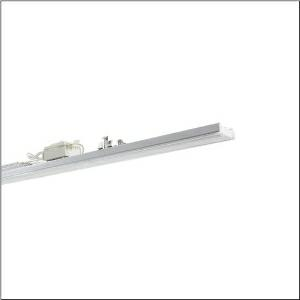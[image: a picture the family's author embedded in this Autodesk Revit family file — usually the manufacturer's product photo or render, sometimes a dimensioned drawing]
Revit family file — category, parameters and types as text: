
# Revit family: licross_r__21_recessed_ho_52te11mn4fxs_d685
name_source: partatom
category: Lighting Fixtures
units: mm (PartAtom-declared; Revit-internal decimal feet)

## family parameters
Cut with Voids When Loaded = No
Host = Face
Light Source = No
Part Type = Normal
Room Calculation Point = No
Round Connector Dimension = Use Diameter
Shared = No

## types (1)
- --- (1 x LED, 15070 lm, 83.1 W, 4000K)
    Apparent Load = 83 VA
    CIE Flux Codes = 87 95 99 100 100
    Color Rendering = 80
    Color Temperature = 4000K
    Default Elevation = 1800 mm
    Description = Licross® 21 Recessed HO, luminaire insert, of sheet steel, galvanised, coil coated, white, length: 1.500mm, width: 66mm, height: 67mm, LED rated luminous flux: 15.060lm, light colour: 840, control gear: ON/OFF Multilumen, with plug, 3-pole, with phase selection, mains connection: 220..240V, AC, 50/60Hz, rated input power: 83W, internal wiring halogen-free, primary light control with lens, of plastic, primary optical cover: cover, of PMMA, light emission: direct distribution, primary light characteristic: symmetric, protection rating (complete): IP54, insulation class (complete): insulation class I (protective earthing), certification: CE, ENEC, VDE, UKCA, protection symbol: D if used in an environment with non-conductive dust loads with corresponding accessories, impact resistance: IK06, permissible ambient temperature for indoor applications: -35..+30°C, corresponds to IFS (International Featured Standards) requirements for safety and quality in the food industry, reducing of maximum allowable ambient temperature of 5°C with ceiling mounting, LABS conformity tested according to VDMA 24364:2018-05, packaging unit: 1 piece
    Height = 58 mm
    Lamp = 1 x LED
    Lamp Light Flux = 15070 lm
    Lamp Power = 83.1 W
    Lamp count = 1
    Length = 1500 mm
    Luminous efficacy = 181 lm/W
    Manufacturer = Siteco
    ModVariant = No
    Model = 52TE11MN4FXS
    Mounting Place = Ceiling
    Mounting Type = Pendant
    Number of Poles = 1
    OnlyDefault = Yes
    Power Factor = 1
    Product Name = Licross® 21 Recessed HO
    Product group = luminaire insert | ceiling pendant
    ProductGroupID = 902
    Protection Class = Protection class I
    Protection Degree = IP 54
    RLX_Detail_Level = 1
    RLX_Emergency_Light_Flux = 0 lm
    RLX_Emergency_Type = 0
    RLX_Emergency_Type_DB = No
    RlxData = <blob elided: 22249 chars, md5=fcd3a372>
    Socket = socket
    Standby Power = 0 W
    System Light Flux = 15070 lm
    System Power = 83 W
    Type Comments = factory setting: luminous flux: 100 % | (A | C | E) | 195 mA
    Type Image = l_1296930.jpg
    URL = http://relux.com
    VarID = @adj_129483
    Voltage = 0 V
    Weight = 0.00 kg
    Width = 66 mm

## geometry (parser evidence)
native form markers: Blend x4, Sweep x9
no freeform markers — native parametric forms only
